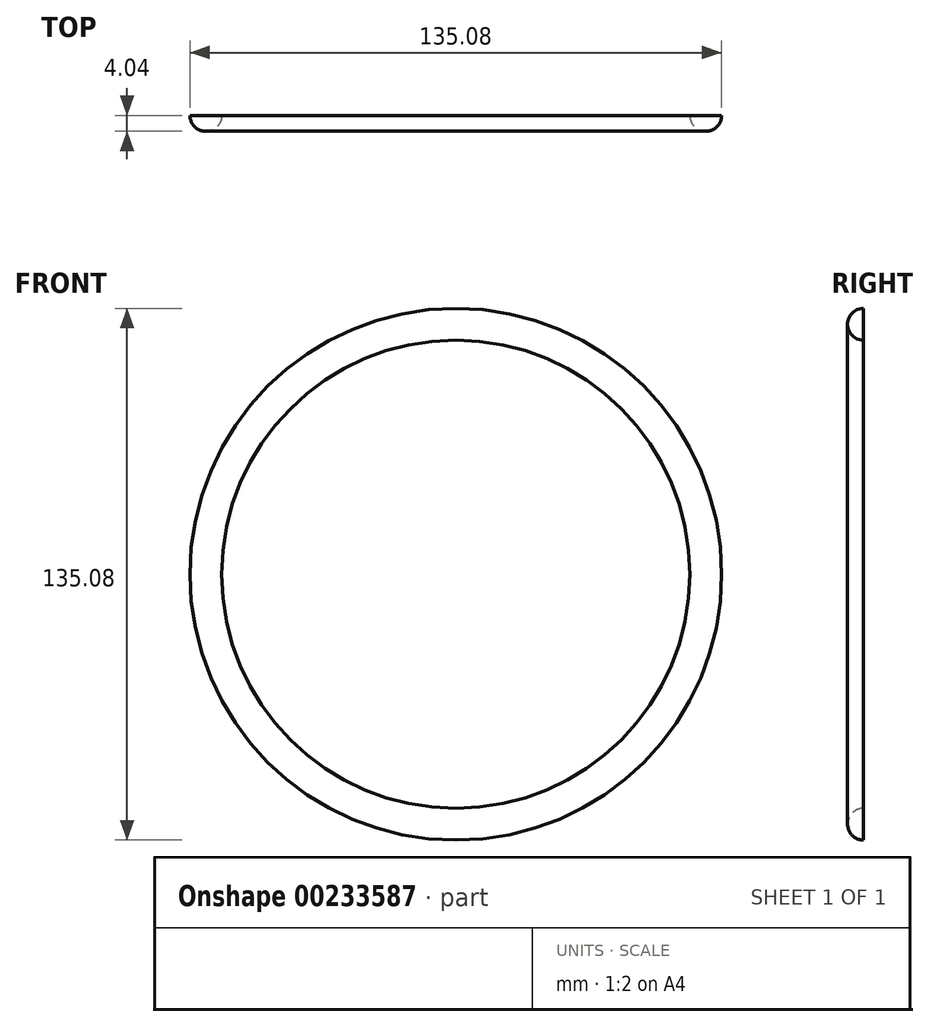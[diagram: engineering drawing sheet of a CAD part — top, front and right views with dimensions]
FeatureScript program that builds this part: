
annotation { "Feature Type Name" : "Feature", "Feature Type Description" : "" }
export const myFeature = defineFeature(function(context is Context, id is Id, definition is map)
    precondition{}
    {
        {
            var Q0;
            Q0=qCreatedBy(makeId("Front.planeOp"),FACE);
            var sketch = newSketch(context, id + "F0", { "sketchPlane" : qUnion([Q0])});
            skCircle(sketch, "E0", {"center": v(0, 0) * mm, "radius": 63.5 * mm});
            skSolve(sketch);
        }
        {
            var Q0;
            Q0=qCreatedBy(makeId("Right.planeOp"),FACE);
            var sketch = newSketch(context, id + "F1", { "sketchPlane" : qUnion([Q0])});
            skArc(sketch, "E1", {"start": v(0, 67.54) * mm, "mid": v(-4.04, 63.5) * mm, "end": v(0, 59.46) * mm});
            skLineSegment(sketch, "E2", {"start": v(0, 67.54) * mm, "end": v(0, 59.46) * mm});
            skSolve(sketch);
        }
        {
            var Q0;
            Q0=makeQuery(id+"F1.imprint","IMPRINT",FACE,{"disambiguationData":[TD([[makeQuery(id+"F1.imprint","IMPRINT",EDGE,{"derivedFrom":sQuery(id+"F1.wireOp",EDGE,"E1")}),1.0]])]});
            var Q1;
            Q1=sQuery(id+"F0.wireOp",EDGE,"E0");
            revolve(context, id + "F2", {"entities" : qUnion([Q0]), "axis" : qUnion([Q1]), "revolveType" : RevolveType.FULL});
        }
    });
